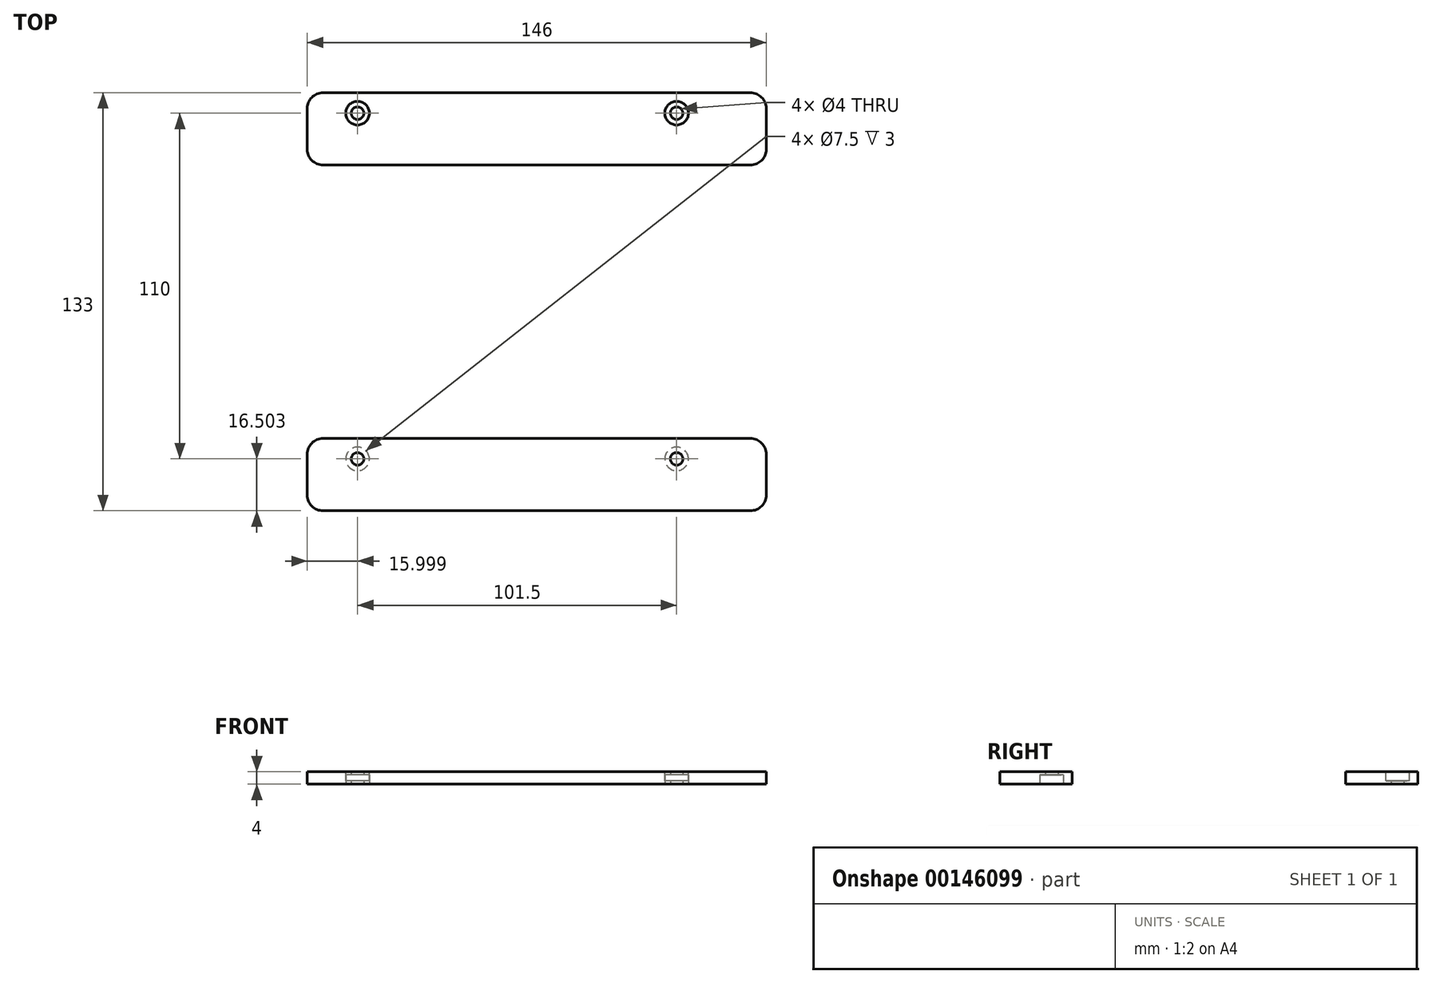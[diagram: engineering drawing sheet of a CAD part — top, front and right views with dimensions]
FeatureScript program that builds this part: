
annotation { "Feature Type Name" : "Feature", "Feature Type Description" : "" }
export const myFeature = defineFeature(function(context is Context, id is Id, definition is map)
    precondition{}
    {
        {
            var Q0;
            Q0=qCreatedBy(makeId("Top.planeOp"),FACE);
            var sketch = newSketch(context, id + "F0", { "sketchPlane" : qUnion([Q0])});
            skLineSegment(sketch, "E0.bottom", {"start": v(-84.1, -26.3) * mm, "end": v(61.9, -26.3) * mm});
            skLineSegment(sketch, "E0.top", {"start": v(-84.1, -49.3) * mm, "end": v(61.9, -49.3) * mm});
            skLineSegment(sketch, "E0.left", {"start": v(-84.1, -26.3) * mm, "end": v(-84.1, -49.3) * mm});
            skLineSegment(sketch, "E0.right", {"start": v(61.9, -26.3) * mm, "end": v(61.9, -49.3) * mm});
            skCircle(sketch, "E1", {"center": v(-68.1, -32.8) * mm, "radius": 3.75 * mm});
            skCircle(sketch, "E2", {"center": v(33.4, -32.8) * mm, "radius": 3.75 * mm});
            skCircle(sketch, "E3", {"center": v(-68.1, -32.8) * mm, "radius": 2 * mm});
            skCircle(sketch, "E4", {"center": v(33.4, -32.8) * mm, "radius": 2 * mm});
            skLineSegment(sketch, "E5.bottom", {"start": v(-84.1, -26.3) * mm, "end": v(-64.1, -26.3) * mm});
            skLineSegment(sketch, "E5.top", {"start": v(-84.1, 11.7) * mm, "end": v(-64.1, 11.7) * mm});
            skLineSegment(sketch, "E5.left", {"start": v(-84.1, -26.3) * mm, "end": v(-84.1, 11.7) * mm});
            skLineSegment(sketch, "E5.right", {"start": v(-64.1, -26.3) * mm, "end": v(-64.1, 11.7) * mm});
            skLineSegment(sketch, "E6.bottom", {"start": v(-84.1, -49.3) * mm, "end": v(-64.1, -49.3) * mm});
            skLineSegment(sketch, "E6.top", {"start": v(-84.1, -87.3) * mm, "end": v(-64.1, -87.3) * mm});
            skLineSegment(sketch, "E6.left", {"start": v(-84.1, -49.3) * mm, "end": v(-84.1, -87.3) * mm});
            skLineSegment(sketch, "E6.right", {"start": v(-64.1, -49.3) * mm, "end": v(-64.1, -87.3) * mm});
            skLineSegment(sketch, "E7.bottom", {"start": v(61.9, -26.3) * mm, "end": v(41.9, -26.3) * mm});
            skLineSegment(sketch, "E7.top", {"start": v(61.9, 11.7) * mm, "end": v(41.9, 11.7) * mm});
            skLineSegment(sketch, "E7.left", {"start": v(61.9, -26.3) * mm, "end": v(61.9, 11.7) * mm});
            skLineSegment(sketch, "E7.right", {"start": v(41.9, -26.3) * mm, "end": v(41.9, 11.7) * mm});
            skLineSegment(sketch, "E8.bottom", {"start": v(61.9, -49.3) * mm, "end": v(41.9, -49.3) * mm});
            skLineSegment(sketch, "E8.top", {"start": v(61.9, -87.3) * mm, "end": v(41.9, -87.3) * mm});
            skLineSegment(sketch, "E8.left", {"start": v(61.9, -49.3) * mm, "end": v(61.9, -87.3) * mm});
            skLineSegment(sketch, "E8.right", {"start": v(41.9, -49.3) * mm, "end": v(41.9, -87.3) * mm});
            skSolve(sketch);
        }
        {
            var Q0;
            Q0=makeQuery(id+"F0.imprint","IMPRINT",FACE,{"disambiguationData":[TD([[makeQuery(id+"F0.imprint","IMPRINT",EDGE,{"derivedFrom":sQuery(id+"F0.wireOp",EDGE,"E5.bottom")}),1.0]])]});
            var Q1;
            Q1=makeQuery(id+"F0.imprint","IMPRINT",FACE,{"disambiguationData":[TD([[makeQuery(id+"F0.imprint","IMPRINT",EDGE,{"derivedFrom":sQuery(id+"F0.wireOp",EDGE,"E6.bottom")}),-1.0]])]});
            var Q2;
            Q2=makeQuery(id+"F0.imprint","IMPRINT",FACE,{"disambiguationData":[TD([[makeQuery(id+"F0.imprint","IMPRINT",EDGE,{"derivedFrom":sQuery(id+"F0.wireOp",EDGE,"E0.bottom")}),-1.0]])]});
            var Q3;
            Q3=makeQuery(id+"F0.imprint","IMPRINT",FACE,{"disambiguationData":[TD([[makeQuery(id+"F0.imprint","IMPRINT",EDGE,{"derivedFrom":sQuery(id+"F0.wireOp",EDGE,"E7.bottom")}),-1.0]])]});
            var Q4;
            Q4=makeQuery(id+"F0.imprint","IMPRINT",FACE,{"disambiguationData":[TD([[makeQuery(id+"F0.imprint","IMPRINT",EDGE,{"derivedFrom":sQuery(id+"F0.wireOp",EDGE,"E8.bottom")}),1.0]])]});
            var Q5;
            Q5=makeQuery(id+"F0.imprint","IMPRINT",FACE,{"disambiguationData":[TD([[makeQuery(id+"F0.imprint","IMPRINT",EDGE,{"derivedFrom":sQuery(id+"F0.wireOp",EDGE,"E1")}),1.0]])]});
            var Q6;
            Q6=makeQuery(id+"F0.imprint","IMPRINT",FACE,{"disambiguationData":[TD([[makeQuery(id+"F0.imprint","IMPRINT",EDGE,{"derivedFrom":sQuery(id+"F0.wireOp",EDGE,"E2")}),1.0]])]});
            extrude(context, id + "F1", {"entities" : qUnion([Q0, Q1, Q2, Q3, Q4, Q5, Q6]), "depth" : 4 * mm});
        }
        {
            var Q0;
            Q0=makeQuery(id+"F1.opExtrude","SWEPT_EDGE",EDGE,{"disambiguationData":[OSD([sQuery(id+"F0.wireOp",EDGE,"E0.top"),sQuery(id+"F0.wireOp",EDGE,"E6.bottom"),sQuery(id+"F0.wireOp",EDGE,"E6.right")])]});
            var Q1;
            Q1=makeQuery(id+"F1.opExtrude","SWEPT_EDGE",EDGE,{"disambiguationData":[OSD([sQuery(id+"F0.wireOp",EDGE,"E6.top"),sQuery(id+"F0.wireOp",EDGE,"E6.right")])]});
            var Q2;
            Q2=makeQuery(id+"F1.opExtrude","SWEPT_EDGE",EDGE,{"disambiguationData":[OSD([sQuery(id+"F0.wireOp",EDGE,"E8.top"),sQuery(id+"F0.wireOp",EDGE,"E8.right")])]});
            var Q3;
            Q3=makeQuery(id+"F1.opExtrude","SWEPT_EDGE",EDGE,{"disambiguationData":[OSD([sQuery(id+"F0.wireOp",EDGE,"E8.top"),sQuery(id+"F0.wireOp",EDGE,"E8.left")])]});
            var Q4;
            Q4=makeQuery(id+"F1.opExtrude","SWEPT_EDGE",EDGE,{"disambiguationData":[OSD([sQuery(id+"F0.wireOp",EDGE,"E6.top"),sQuery(id+"F0.wireOp",EDGE,"E6.left")])]});
            var Q5;
            Q5=makeQuery(id+"F1.opExtrude","SWEPT_EDGE",EDGE,{"disambiguationData":[OSD([sQuery(id+"F0.wireOp",EDGE,"E0.bottom"),sQuery(id+"F0.wireOp",EDGE,"E5.bottom"),sQuery(id+"F0.wireOp",EDGE,"E5.right")])]});
            var Q6;
            Q6=makeQuery(id+"F1.opExtrude","SWEPT_EDGE",EDGE,{"disambiguationData":[OSD([sQuery(id+"F0.wireOp",EDGE,"E5.top"),sQuery(id+"F0.wireOp",EDGE,"E5.left")])]});
            var Q7;
            Q7=makeQuery(id+"F1.opExtrude","SWEPT_EDGE",EDGE,{"disambiguationData":[OSD([sQuery(id+"F0.wireOp",EDGE,"E5.top"),sQuery(id+"F0.wireOp",EDGE,"E5.right")])]});
            var Q8;
            Q8=makeQuery(id+"F1.opExtrude","SWEPT_EDGE",EDGE,{"disambiguationData":[OSD([sQuery(id+"F0.wireOp",EDGE,"E0.bottom"),sQuery(id+"F0.wireOp",EDGE,"E7.bottom"),sQuery(id+"F0.wireOp",EDGE,"E7.right")])]});
            var Q9;
            Q9=makeQuery(id+"F1.opExtrude","SWEPT_EDGE",EDGE,{"disambiguationData":[OSD([sQuery(id+"F0.wireOp",EDGE,"E7.top"),sQuery(id+"F0.wireOp",EDGE,"E7.right")])]});
            var Q10;
            Q10=makeQuery(id+"F1.opExtrude","SWEPT_EDGE",EDGE,{"disambiguationData":[OSD([sQuery(id+"F0.wireOp",EDGE,"E7.top"),sQuery(id+"F0.wireOp",EDGE,"E7.left")])]});
            var Q11;
            Q11=makeQuery(id+"F1.opExtrude","SWEPT_EDGE",EDGE,{"disambiguationData":[OSD([sQuery(id+"F0.wireOp",EDGE,"E0.top"),sQuery(id+"F0.wireOp",EDGE,"E8.bottom"),sQuery(id+"F0.wireOp",EDGE,"E8.right")])]});
            fillet(context, id + "F2", {"entities" : qUnion([Q0, Q1, Q2, Q3, Q4, Q5, Q6, Q7, Q8, Q9, Q10, Q11]), "radius" : 5 * mm, "tangentPropagation" : true, "allowEdgeOverflow" : false});
        }
        {
            var Q0;
            Q0=makeQuery(id+"F1.opExtrude","SWEPT_BODY",BODY,{"disambiguationData":[OSD([sQuery(id+"F0.wireOp",EDGE,"E0.bottom"),sQuery(id+"F0.wireOp",EDGE,"E0.top"),sQuery(id+"F0.wireOp",EDGE,"E0.left"),sQuery(id+"F0.wireOp",EDGE,"E0.right"),sQuery(id+"F0.wireOp",EDGE,"E3"),sQuery(id+"F0.wireOp",EDGE,"E4"),sQuery(id+"F0.wireOp",EDGE,"E5.top"),sQuery(id+"F0.wireOp",EDGE,"E5.left"),sQuery(id+"F0.wireOp",EDGE,"E5.right"),sQuery(id+"F0.wireOp",EDGE,"E6.top"),sQuery(id+"F0.wireOp",EDGE,"E6.left"),sQuery(id+"F0.wireOp",EDGE,"E6.right"),sQuery(id+"F0.wireOp",EDGE,"E7.top"),sQuery(id+"F0.wireOp",EDGE,"E7.left"),sQuery(id+"F0.wireOp",EDGE,"E7.right"),sQuery(id+"F0.wireOp",EDGE,"E8.top"),sQuery(id+"F0.wireOp",EDGE,"E8.left"),sQuery(id+"F0.wireOp",EDGE,"E8.right")])]});
            transform(context, id + "F3", {"entities" : qUnion([Q0]), "transformType" : TransformType.COPY});
        }
        {
            var Q0;
            Q0=makeQuery(id+"F3.opPattern","COPY",BODY,{"derivedFrom":makeQuery(id+"F1.opExtrude","SWEPT_BODY",BODY,{"disambiguationData":[OSD([sQuery(id+"F0.wireOp",EDGE,"E0.bottom"),sQuery(id+"F0.wireOp",EDGE,"E0.top"),sQuery(id+"F0.wireOp",EDGE,"E0.left"),sQuery(id+"F0.wireOp",EDGE,"E0.right"),sQuery(id+"F0.wireOp",EDGE,"E3"),sQuery(id+"F0.wireOp",EDGE,"E4"),sQuery(id+"F0.wireOp",EDGE,"E5.top"),sQuery(id+"F0.wireOp",EDGE,"E5.left"),sQuery(id+"F0.wireOp",EDGE,"E5.right"),sQuery(id+"F0.wireOp",EDGE,"E6.top"),sQuery(id+"F0.wireOp",EDGE,"E6.left"),sQuery(id+"F0.wireOp",EDGE,"E6.right"),sQuery(id+"F0.wireOp",EDGE,"E7.top"),sQuery(id+"F0.wireOp",EDGE,"E7.left"),sQuery(id+"F0.wireOp",EDGE,"E7.right"),sQuery(id+"F0.wireOp",EDGE,"E8.top"),sQuery(id+"F0.wireOp",EDGE,"E8.left"),sQuery(id+"F0.wireOp",EDGE,"E8.right")])]}),"instanceName":"1"});
            transform(context, id + "F4", {"entities" : qUnion([Q0]), "transformType" : TransformType.TRANSLATION_3D, "dx" : 0 * mm, "dy" : 110 * mm, "dz" : 0 * mm, "makeCopy" : false});
        }
        {
            var Q0;
            Q0=makeQuery(id+"F0.imprint","IMPRINT",FACE,{"disambiguationData":[TD([[makeQuery(id+"F0.imprint","IMPRINT",EDGE,{"derivedFrom":sQuery(id+"F0.wireOp",EDGE,"E1")}),1.0]])]});
            var Q1;
            Q1=makeQuery(id+"F0.imprint","IMPRINT",FACE,{"disambiguationData":[TD([[makeQuery(id+"F0.imprint","IMPRINT",EDGE,{"derivedFrom":sQuery(id+"F0.wireOp",EDGE,"E2")}),1.0]])]});
            extrude(context, id + "F5", {"entities" : qUnion([Q0, Q1]), "operationType" : NewBodyOperationType.REMOVE, "depth" : 3 * mm});
        }
        {
            var Q0;
            Q0=makeQuery(id+"F3.opPattern","COPY",FACE,{"derivedFrom":makeQuery(id+"F1.opExtrude","CAP_FACE",FACE,{"disambiguationData":[OSD([sQuery(id+"F0.wireOp",EDGE,"E0.bottom"),sQuery(id+"F0.wireOp",EDGE,"E0.top"),sQuery(id+"F0.wireOp",EDGE,"E0.left"),sQuery(id+"F0.wireOp",EDGE,"E0.right"),sQuery(id+"F0.wireOp",EDGE,"E3"),sQuery(id+"F0.wireOp",EDGE,"E4"),sQuery(id+"F0.wireOp",EDGE,"E5.top"),sQuery(id+"F0.wireOp",EDGE,"E5.left"),sQuery(id+"F0.wireOp",EDGE,"E5.right"),sQuery(id+"F0.wireOp",EDGE,"E6.top"),sQuery(id+"F0.wireOp",EDGE,"E6.left"),sQuery(id+"F0.wireOp",EDGE,"E6.right"),sQuery(id+"F0.wireOp",EDGE,"E7.top"),sQuery(id+"F0.wireOp",EDGE,"E7.left"),sQuery(id+"F0.wireOp",EDGE,"E7.right"),sQuery(id+"F0.wireOp",EDGE,"E8.top"),sQuery(id+"F0.wireOp",EDGE,"E8.left"),sQuery(id+"F0.wireOp",EDGE,"E8.right")])],"isStart":false}),"instanceName":"1"});
            var sketch = newSketch(context, id + "F6", { "sketchPlane" : qUnion([Q0])});
            skCircle(sketch, "E9", {"center": v(-68.1, 77.2) * mm, "radius": 3.75 * mm});
            skCircle(sketch, "E10", {"center": v(33.4, 77.2) * mm, "radius": 3.75 * mm});
            skSolve(sketch);
        }
        {
            var Q0;
            Q0=makeQuery(id+"F6.imprint","IMPRINT",FACE,{"disambiguationData":[TD([[makeQuery(id+"F6.imprint","IMPRINT",EDGE,{"derivedFrom":sQuery(id+"F6.wireOp",EDGE,"E9")}),1.0]])]});
            var Q1;
            Q1=makeQuery(id+"F6.imprint","IMPRINT",FACE,{"disambiguationData":[TD([[makeQuery(id+"F6.imprint","IMPRINT",EDGE,{"derivedFrom":sQuery(id+"F6.wireOp",EDGE,"E10")}),1.0]])]});
            extrude(context, id + "F7", {"entities" : qUnion([Q0, Q1]), "operationType" : NewBodyOperationType.REMOVE, "oppositeDirection" : true, "depth" : 3 * mm});
        }
    });
